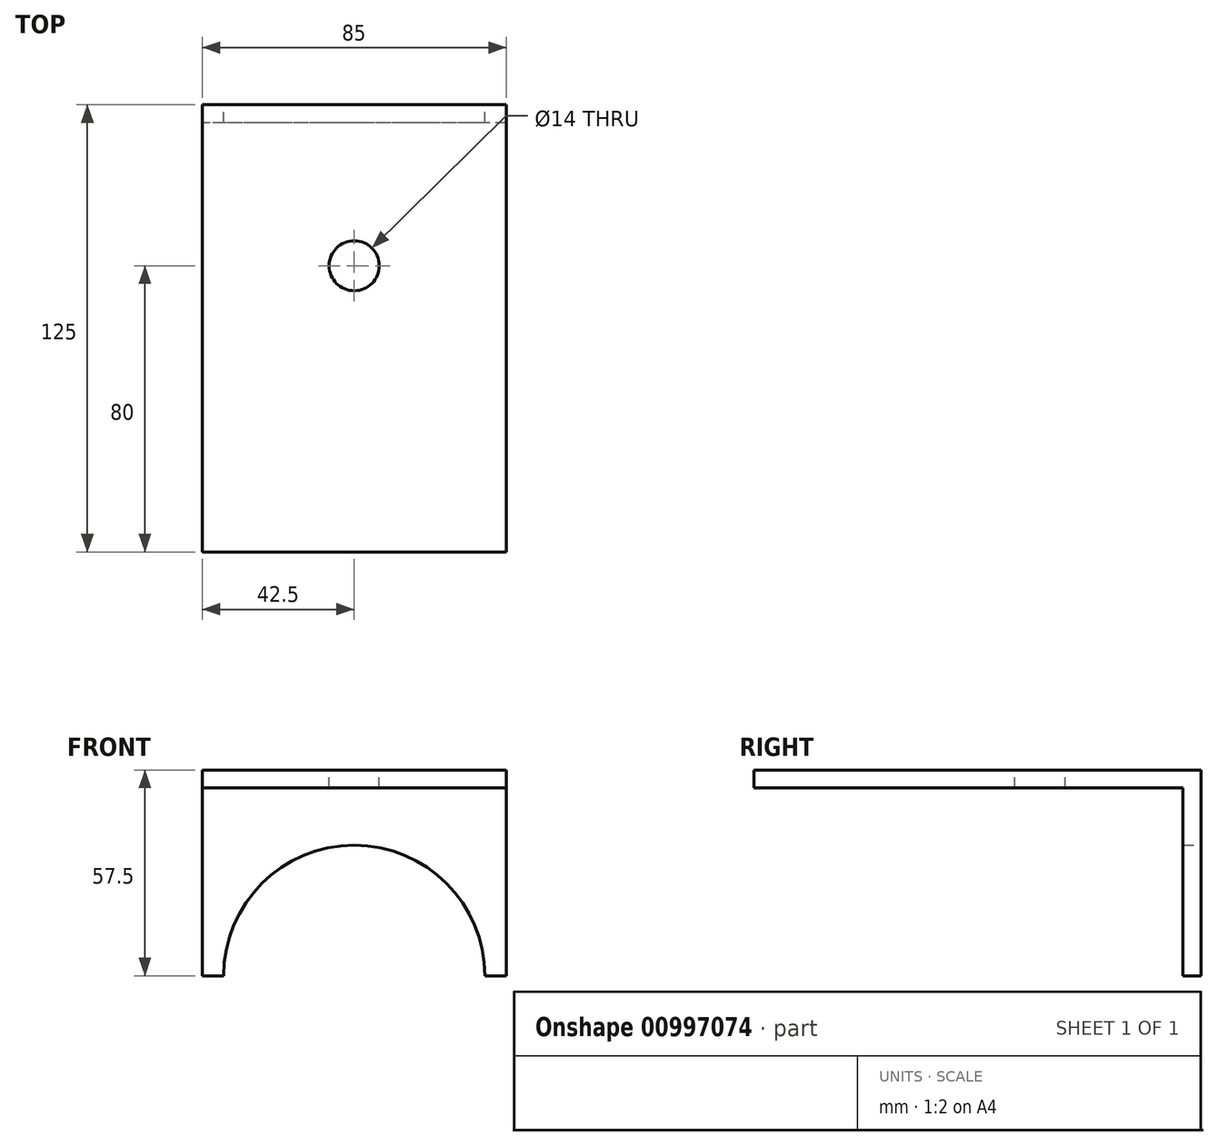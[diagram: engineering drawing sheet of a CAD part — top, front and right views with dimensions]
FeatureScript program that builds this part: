
annotation { "Feature Type Name" : "Feature", "Feature Type Description" : "" }
export const myFeature = defineFeature(function(context is Context, id is Id, definition is map)
    precondition{}
    {
        {
            var Q0;
            Q0=qCreatedBy(makeId("Front.planeOp"),FACE);
            var sketch = newSketch(context, id + "F0", { "sketchPlane" : qUnion([Q0])});
            skArc(sketch, "E0", {"start": v(36.5, 0) * mm, "mid": v(0, 36.5) * mm, "end": v(-36.5, 0) * mm});
            skLineSegment(sketch, "E1", {"start": v(-36.5, 0) * mm, "end": v(-42.5, 0) * mm});
            skLineSegment(sketch, "E2", {"start": v(-42.5, 0) * mm, "end": v(-42.5, 57.5) * mm});
            skLineSegment(sketch, "E3", {"start": v(-42.5, 57.5) * mm, "end": v(42.5, 57.5) * mm});
            skLineSegment(sketch, "E4", {"start": v(42.5, 57.5) * mm, "end": v(42.5, 0) * mm});
            skLineSegment(sketch, "E5", {"start": v(42.5, 0) * mm, "end": v(36.5, 0) * mm});
            skSolve(sketch);
        }
        {
            var Q0;
            Q0=qSketchRegion(id+"F0",true);
            extrude(context, id + "F1", {"entities" : qUnion([Q0]), "depth" : 5 * mm, "offsetDistance" : 25 * mm});
        }
        {
            var Q0;
            Q0=makeQuery(id+"F1.opExtrude","SWEPT_FACE",FACE,{"disambiguationData":[OSD([sQuery(id+"F0.wireOp",EDGE,"E3")])]});
            var sketch = newSketch(context, id + "F2", { "sketchPlane" : qUnion([Q0])});
            skPoint(sketch, "E6.oppositeSnap0", {"position": v(42.5, -2.5) * mm});
            skLineSegment(sketch, "E6.bottom", {"start": v(-42.5, 0) * mm, "end": v(42.5, 0) * mm});
            skLineSegment(sketch, "E6.top", {"start": v(-42.5, -125) * mm, "end": v(42.5, -125) * mm});
            skLineSegment(sketch, "E6.left", {"start": v(-42.5, 0) * mm, "end": v(-42.5, -125) * mm});
            skLineSegment(sketch, "E6.right", {"start": v(42.5, 0) * mm, "end": v(42.5, -125) * mm});
            skCircle(sketch, "E7", {"center": v(0, -45) * mm, "radius": 7 * mm});
            skSolve(sketch);
        }
        {
            var Q0;
            Q0=qSketchRegion(id+"F2",true);
            extrude(context, id + "F3", {"entities" : qUnion([Q0]), "operationType" : NewBodyOperationType.ADD, "oppositeDirection" : true, "depth" : 5 * mm, "offsetDistance" : 25 * mm});
        }
    });
